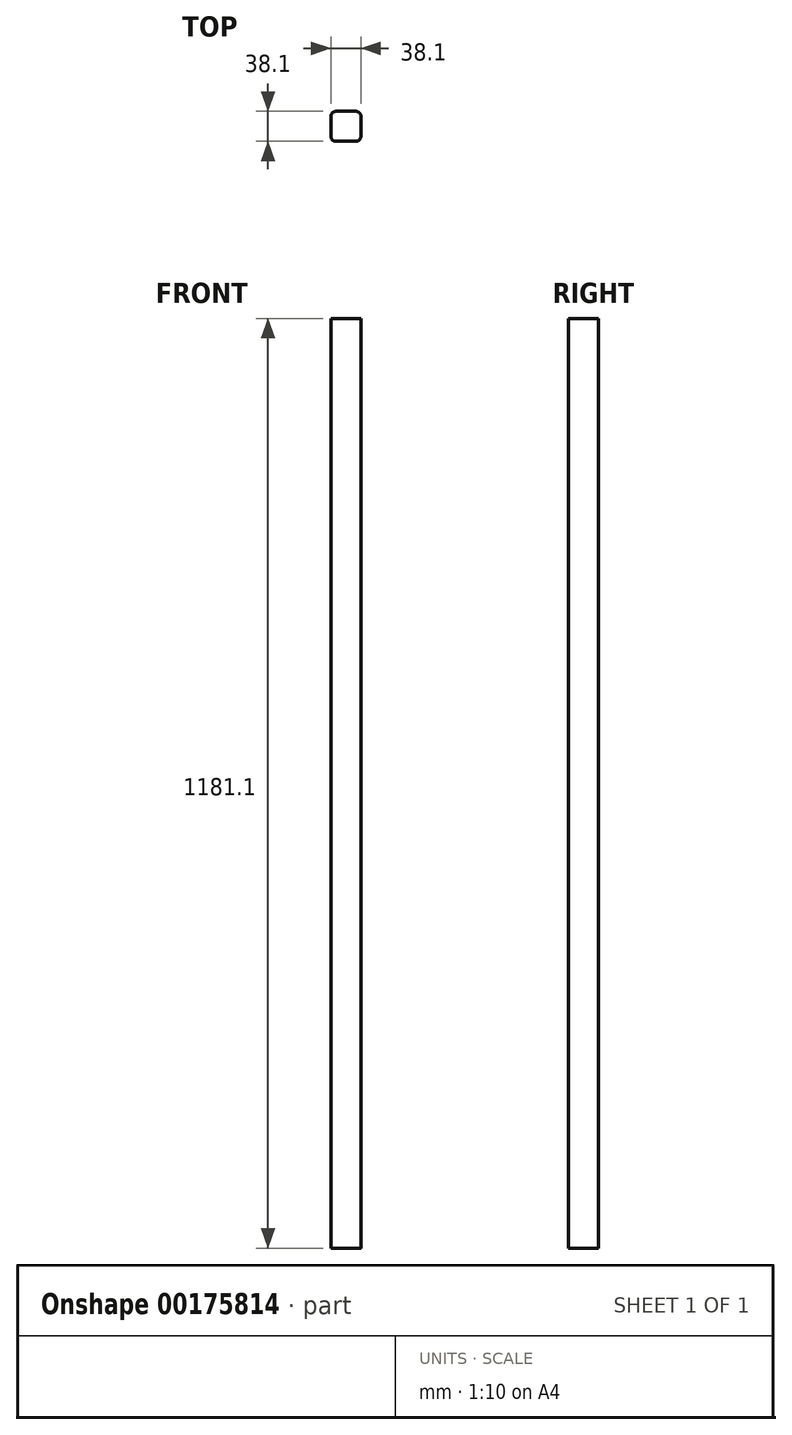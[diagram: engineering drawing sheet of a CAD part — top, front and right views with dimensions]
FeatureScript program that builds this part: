
annotation { "Feature Type Name" : "Feature", "Feature Type Description" : "" }
export const myFeature = defineFeature(function(context is Context, id is Id, definition is map)
    precondition{}
    {
        {
            var Q0;
            Q0=qCreatedBy(makeId("Top.planeOp"),FACE);
            var sketch = newSketch(context, id + "F0", { "sketchPlane" : qUnion([Q0])});
            skLineSegment(sketch, "E0.bottom", {"start": v(12.7, 19.05) * mm, "end": v(-12.7, 19.05) * mm});
            skLineSegment(sketch, "E0.top", {"start": v(12.7, -19.05) * mm, "end": v(-12.7, -19.05) * mm});
            skLineSegment(sketch, "E0.left", {"start": v(19.05, 12.7) * mm, "end": v(19.05, -12.7) * mm});
            skLineSegment(sketch, "E0.right", {"start": v(-19.05, 12.7) * mm, "end": v(-19.05, -12.7) * mm});
            skPoint(sketch, "E0.middle", {"position": v(0, 0) * mm});
            skPoint(sketch, "E1.visualSharp", {"position": v(-19.05, 19.05) * mm});
            skArc(sketch, "E1.filletArc", {"start": v(-12.7, 19.05) * mm, "mid": v(-17.2, 17.2) * mm, "end": v(-19.05, 12.7) * mm});
            skPoint(sketch, "E2.visualSharp", {"position": v(19.05, 19.05) * mm});
            skArc(sketch, "E2.filletArc", {"start": v(19.05, 12.7) * mm, "mid": v(17.2, 17.2) * mm, "end": v(12.7, 19.05) * mm});
            skPoint(sketch, "E3.visualSharp", {"position": v(19.05, -19.05) * mm});
            skArc(sketch, "E3.filletArc", {"start": v(12.7, -19.05) * mm, "mid": v(17.2, -17.2) * mm, "end": v(19.05, -12.7) * mm});
            skPoint(sketch, "E4.visualSharp", {"position": v(-19.05, -19.05) * mm});
            skArc(sketch, "E4.filletArc", {"start": v(-19.05, -12.7) * mm, "mid": v(-17.2, -17.2) * mm, "end": v(-12.7, -19.05) * mm});
            skSolve(sketch);
        }
        {
            var Q0;
            Q0=qSketchRegion(id+"F0",true);
            extrude(context, id + "F1", {"entities" : qUnion([Q0]), "depth" : 1181.1 * mm, "offsetDistance" : 25.4 * mm});
        }
    });
